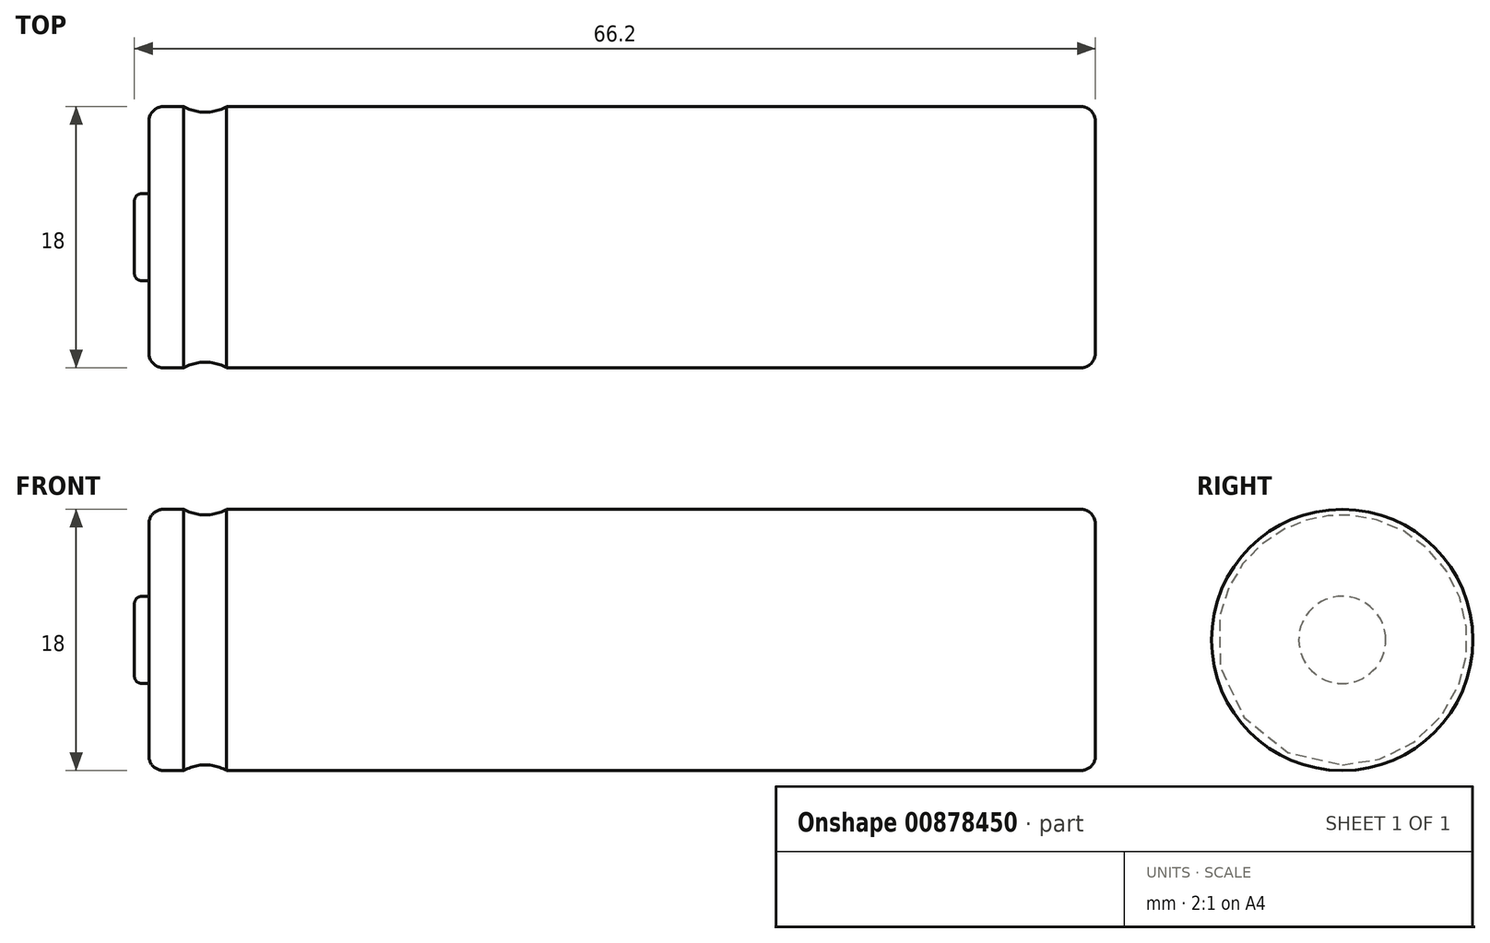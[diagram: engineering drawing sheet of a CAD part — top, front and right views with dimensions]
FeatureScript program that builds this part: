
annotation { "Feature Type Name" : "Feature", "Feature Type Description" : "" }
export const myFeature = defineFeature(function(context is Context, id is Id, definition is map)
    precondition{}
    {
        {
            var Q0;
            Q0=qCreatedBy(makeId("Right.planeOp"),FACE);
            var sketch = newSketch(context, id + "F0", { "sketchPlane" : qUnion([Q0])});
            skCircle(sketch, "E0", {"center": v(0, 0) * mm, "radius": 9 * mm});
            skSolve(sketch);
        }
        {
            var Q0;
            Q0=qSketchRegion(id+"F0",true);
            extrude(context, id + "F1", {"entities" : qUnion([Q0]), "depth" : 65.2 * mm, "offsetDistance" : 25 * mm});
        }
        {
            var Q0;
            Q0=makeQuery(id+"F1.opExtrude","CAP_EDGE",EDGE,{"disambiguationData":[OSD([sQuery(id+"F0.wireOp",EDGE,"E0")])],"isStart":false});
            var Q1;
            Q1=makeQuery(id+"F1.opExtrude","CAP_EDGE",EDGE,{"disambiguationData":[OSD([sQuery(id+"F0.wireOp",EDGE,"E0")])],"isStart":true});
            fillet(context, id + "F2", {"entities" : qUnion([Q0, Q1]), "radius" : 1 * mm, "tangentPropagation" : true, "allowEdgeOverflow" : false});
        }
        {
            var Q0;
            Q0=qCreatedBy(makeId("Right.planeOp"),FACE);
            var sketch = newSketch(context, id + "F3", { "sketchPlane" : qUnion([Q0])});
            skCircle(sketch, "E1", {"center": v(0, 0) * mm, "radius": 3 * mm});
            skSolve(sketch);
        }
        {
            var Q0;
            Q0=qSketchRegion(id+"F3",true);
            extrude(context, id + "F4", {"entities" : qUnion([Q0]), "operationType" : NewBodyOperationType.ADD, "depth" : -1 * mm, "offsetDistance" : 25 * mm});
        }
        {
            var Q0;
            Q0=makeQuery(id+"F4.opExtrude","CAP_EDGE",EDGE,{"disambiguationData":[OSD([sQuery(id+"F3.wireOp",EDGE,"E1")])],"isStart":false});
            fillet(context, id + "F5", {"entities" : qUnion([Q0]), "radius" : .5 * mm, "tangentPropagation" : true, "allowEdgeOverflow" : false});
        }
        {
            var Q0;
            Q0=qCreatedBy(makeId("Front.planeOp"),FACE);
            var sketch = newSketch(context, id + "F6", { "sketchPlane" : qUnion([Q0])});
            skCircle(sketch, "E2", {"center": v(3.88, 11.61) * mm, "radius": 3 * mm});
            skSolve(sketch);
        }
        {
            var Q0;
            Q0=makeQuery(id+"F6.imprint","IMPRINT",FACE,{"disambiguationData":[TD([[makeQuery(id+"F6.imprint","IMPRINT",EDGE,{"derivedFrom":sQuery(id+"F6.wireOp",EDGE,"E2")}),1.0]])]});
            var Q1;
            {var subQ0=sQuery(id+"F0.wireOp",EDGE,"E0");Q1=makeQuery(id+"F2.opFillet","BLEND_EDGE",EDGE,{"blendedFrom":[makeQuery(id+"F1.opExtrude","CAP_EDGE",EDGE,{"disambiguationData":[OSD([subQ0])],"isStart":true}),makeQuery(id+"F1.opExtrude","SWEPT_FACE",FACE,{"disambiguationData":[OSD([subQ0])]})],"blendedInto":[makeQuery(id+"F1.opExtrude","SWEPT_FACE",FACE,{"disambiguationData":[OSD([subQ0])]})]});}
            revolve(context, id + "F7", {"operationType" : NewBodyOperationType.REMOVE, "surfaceOperationType" : NewSurfaceOperationType.NEW, "entities" : qUnion([Q0]), "axis" : qUnion([Q1]), "revolveType" : RevolveType.FULL, "oppositeDirection" : true});
        }
    });
